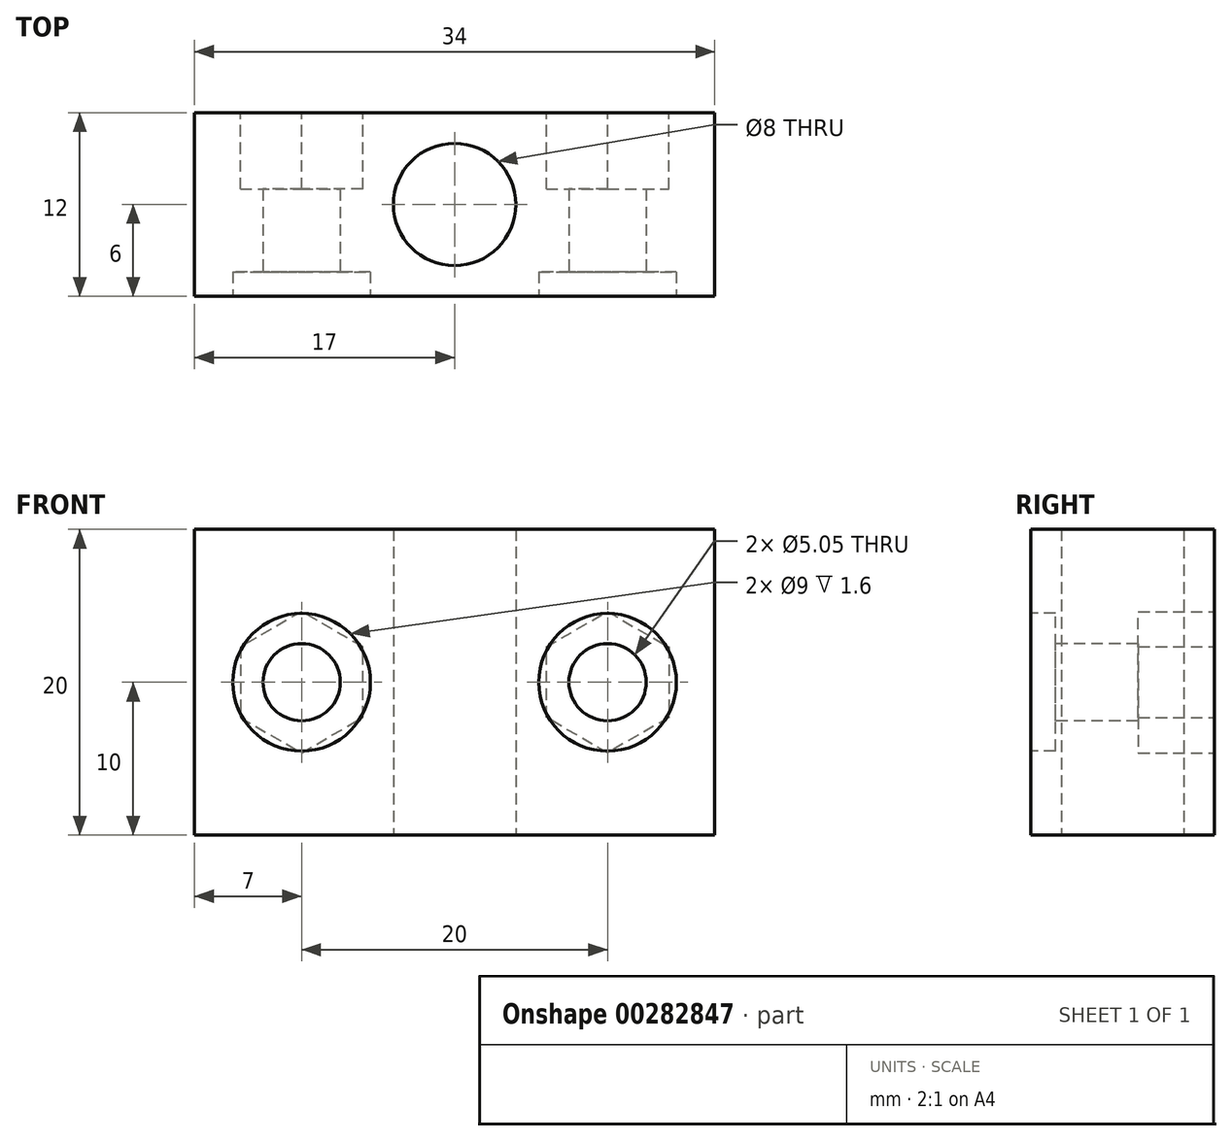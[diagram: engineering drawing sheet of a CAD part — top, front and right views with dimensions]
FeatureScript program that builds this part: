
annotation { "Feature Type Name" : "Feature", "Feature Type Description" : "" }
export const myFeature = defineFeature(function(context is Context, id is Id, definition is map)
    precondition{}
    {
        {
            var Q0;
            Q0=qCreatedBy(makeId("Top.planeOp"),FACE);
            var sketch = newSketch(context, id + "F0", { "sketchPlane" : qUnion([Q0])});
            skLineSegment(sketch, "E0.bottom", {"start": v(17, 6) * mm, "end": v(-17, 6) * mm});
            skLineSegment(sketch, "E0.top", {"start": v(17, -6) * mm, "end": v(-17, -6) * mm});
            skLineSegment(sketch, "E0.left", {"start": v(17, 6) * mm, "end": v(17, -6) * mm});
            skLineSegment(sketch, "E0.right", {"start": v(-17, 6) * mm, "end": v(-17, -6) * mm});
            skPoint(sketch, "E0.middle", {"position": v(0, 0) * mm});
            skCircle(sketch, "E1", {"center": v(0, 0) * mm, "radius": 4 * mm});
            skSolve(sketch);
        }
        {
            var Q0;
            Q0=qSketchRegion(id+"F0",true);
            extrude(context, id + "F1", {"entities" : qUnion([Q0]), "depth" : 20 * mm});
        }
        {
            var Q0;
            Q0=makeQuery(id+"F1.opExtrude","SWEPT_FACE",FACE,{"disambiguationData":[OSD([sQuery(id+"F0.wireOp",EDGE,"E0.top")])]});
            var sketch = newSketch(context, id + "F2", { "sketchPlane" : qUnion([Q0])});
            skCircle(sketch, "E2", {"center": v(-10, 10) * mm, "radius": 2.52 * mm});
            skCircle(sketch, "E3", {"center": v(10, 10) * mm, "radius": 2.52 * mm});
            skLineSegment(sketch, "E4", {"start": v(-17, 10) * mm, "end": v(17, 10) * mm, "construction": true});
            skSolve(sketch);
        }
        {
            var Q0;
            Q0=qSketchRegion(id+"F2",true);
            extrude(context, id + "F3", {"entities" : qUnion([Q0]), "operationType" : NewBodyOperationType.REMOVE, "endBound" : BoundingType.THROUGH_ALL, "oppositeDirection" : true, "depth" : 25 * mm});
        }
        {
            var Q0;
            Q0=makeQuery(id+"F1.opExtrude","SWEPT_FACE",FACE,{"disambiguationData":[OSD([sQuery(id+"F0.wireOp",EDGE,"E0.top")])]});
            var sketch = newSketch(context, id + "F4", { "sketchPlane" : qUnion([Q0])});
            skCircle(sketch, "E5", {"center": v(-10, 10) * mm, "radius": 4.5 * mm});
            skCircle(sketch, "E6", {"center": v(10, 10) * mm, "radius": 4.5 * mm});
            skSolve(sketch);
        }
        {
            var Q0;
            Q0=qSketchRegion(id+"F4",true);
            extrude(context, id + "F5", {"entities" : qUnion([Q0]), "operationType" : NewBodyOperationType.REMOVE, "oppositeDirection" : true, "depth" : 1.6 * mm});
        }
        {
            var Q0;
            Q0=makeQuery(id+"F1.opExtrude","SWEPT_FACE",FACE,{"disambiguationData":[OSD([sQuery(id+"F0.wireOp",EDGE,"E0.bottom")])]});
            var sketch = newSketch(context, id + "F6", { "sketchPlane" : qUnion([Q0])});
            skCircle(sketch, "E7.cCircle", {"center": v(10, 10) * mm, "radius": 4 * mm, "construction": true});
            skLineSegment(sketch, "E7.0", {"start": v(6, 12.3) * mm, "end": v(10, 14.62) * mm});
            skLineSegment(sketch, "E7.1", {"start": v(10, 14.62) * mm, "end": v(14, 12.3) * mm});
            skLineSegment(sketch, "E7.2", {"start": v(14, 12.3) * mm, "end": v(14, 7.7) * mm});
            skLineSegment(sketch, "E7.3", {"start": v(14, 7.7) * mm, "end": v(10, 5.38) * mm});
            skLineSegment(sketch, "E7.4", {"start": v(10, 5.38) * mm, "end": v(6, 7.7) * mm});
            skLineSegment(sketch, "E7.5", {"start": v(6, 7.7) * mm, "end": v(6, 12.3) * mm});
            skPoint(sketch, "E7.0.midPoint", {"position": v(8, 13.46) * mm});
            skLineSegment(sketch, "E8.MirrorCS", {"start": v(-6, 12.3) * mm, "end": v(-10, 14.62) * mm});
            skLineSegment(sketch, "E9.MirrorCS", {"start": v(-6, 7.7) * mm, "end": v(-6, 12.3) * mm});
            skLineSegment(sketch, "E10.MirrorCS", {"start": v(-10, 5.38) * mm, "end": v(-6, 7.7) * mm});
            skLineSegment(sketch, "E11.MirrorCS", {"start": v(-14, 7.7) * mm, "end": v(-10, 5.38) * mm});
            skLineSegment(sketch, "E12.MirrorCS", {"start": v(-14, 12.3) * mm, "end": v(-14, 7.7) * mm});
            skLineSegment(sketch, "E13.MirrorCS", {"start": v(-10, 14.62) * mm, "end": v(-14, 12.3) * mm});
            skCircle(sketch, "E14.MirrorC", {"center": v(-10, 10) * mm, "radius": 4 * mm, "construction": true});
            skPoint(sketch, "E15.MirrorP", {"position": v(-8, 13.46) * mm});
            skSolve(sketch);
        }
        {
            var Q0;
            Q0=qSketchRegion(id+"F6",true);
            extrude(context, id + "F7", {"entities" : qUnion([Q0]), "operationType" : NewBodyOperationType.REMOVE, "oppositeDirection" : true, "depth" : 5 * mm});
        }
    });
